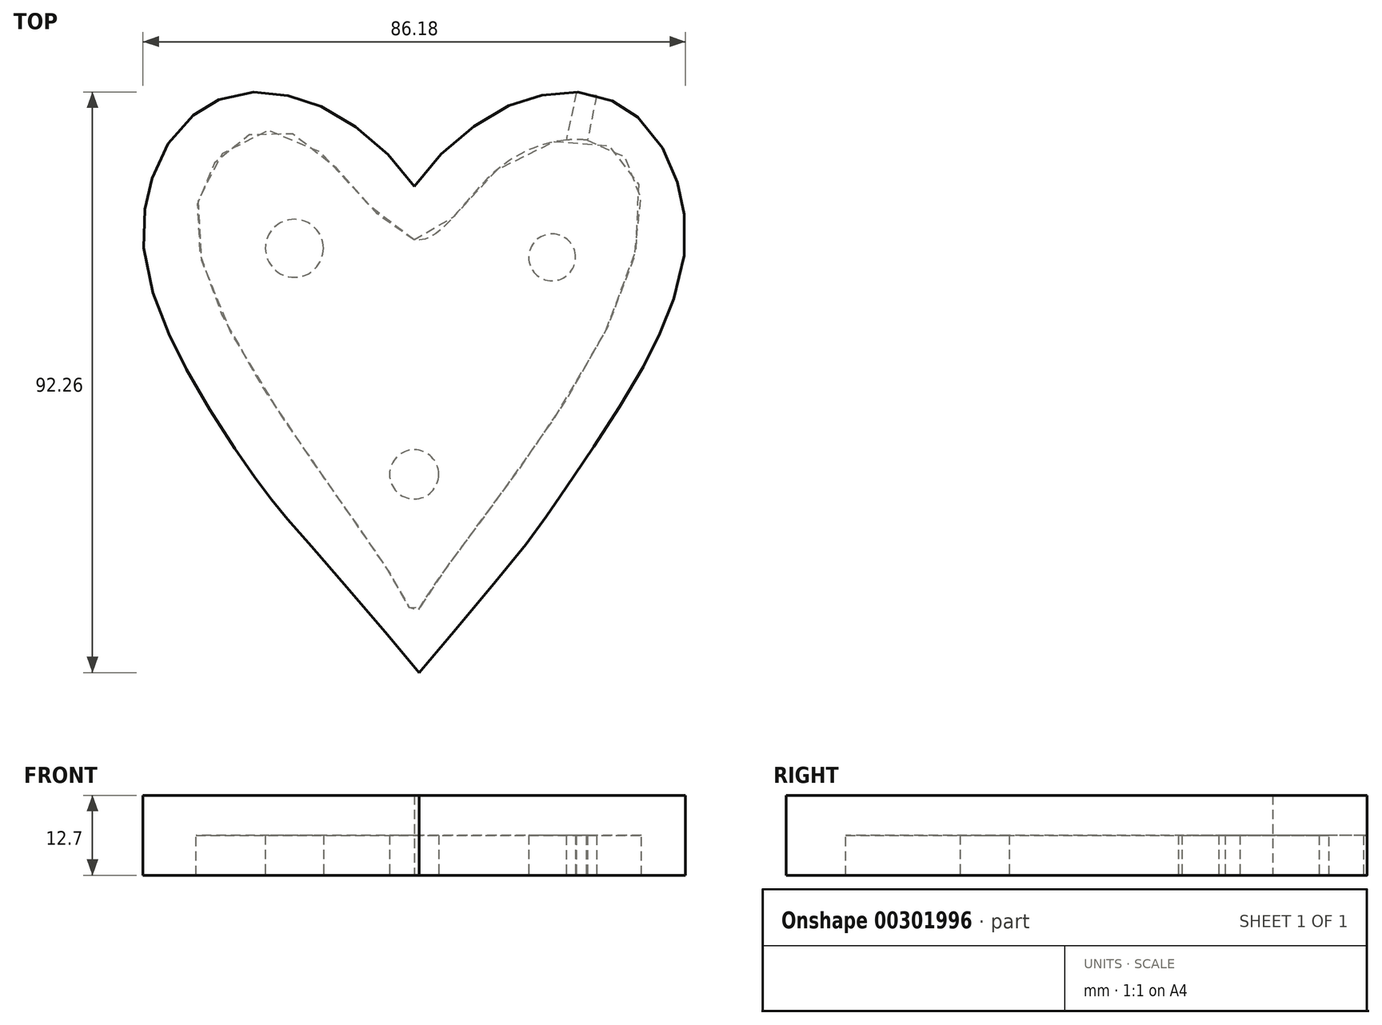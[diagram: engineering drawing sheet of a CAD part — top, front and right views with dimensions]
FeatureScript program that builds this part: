
annotation { "Feature Type Name" : "Feature", "Feature Type Description" : "" }
export const myFeature = defineFeature(function(context is Context, id is Id, definition is map)
    precondition{}
    {
        {
            var Q0;
            Q0=qCreatedBy(makeId("Top.planeOp"),FACE);
            var sketch = newSketch(context, id + "F0", { "sketchPlane" : qUnion([Q0])});
            skFitSpline(sketch, "E0.0", {"points": [v(0.86, 28.46) * mm, v(-0.35, 30.42) * mm, v(-2.59, 33.28) * mm, v(-6.12, 36.72) * mm, v(-8.95, 39.04) * mm, v(-11.94, 41.05) * mm, v(-15.1, 42.7) * mm, v(-17.9, 43.73) * mm, v(-20.24, 44.3) * mm, v(-22.65, 44.72) * mm, v(-25.75, 44.85) * mm, v(-28.85, 44.38) * mm, v(-31.25, 43.54) * mm, v(-33, 42.67) * mm, v(-34.64, 41.54) * mm, v(-36.67, 39.72) * mm, v(-38.89, 36.96) * mm, v(-40.63, 33.71) * mm, v(-41.7, 30.93) * mm, v(-42.31, 28.78) * mm, v(-42.74, 26.58) * mm, v(-43.05, 23.62) * mm, v(-42.96, 19.88) * mm, v(-42.17, 15.33) * mm, v(-40.76, 10.68) * mm, v(-39.13, 6.72) * mm, v(-37.58, 3.5) * mm, v(-35.9, 0.23) * mm, v(-33.58, -3.85) * mm, v(-30.66, -8.55) * mm, v(-28.28, -12.14) * mm, v(-26.49, -14.72) * mm, v(-25.23, -16.49) * mm, v(-24.07, -18.07) * mm, v(-23.06, -19.42) * mm, v(-22.13, -20.6) * mm, v(-21.23, -21.72) * mm, v(-20.28, -22.84) * mm, v(-18.89, -24.45) * mm, v(-16.73, -26.9) * mm, v(-12.94, -31.24) * mm, v(-7.44, -37.65) * mm, v(-2.27, -43.76) * mm, v(0.77, -47.39) * mm]});
            skFitSpline(sketch, "E0.1", {"points": [v(-0.86, 28.46) * mm, v(0.35, 30.42) * mm, v(2.58, 33.28) * mm, v(6.1, 36.7) * mm, v(8.92, 39.02) * mm, v(11.9, 41.03) * mm, v(15.05, 42.68) * mm, v(17.84, 43.71) * mm, v(20.17, 44.3) * mm, v(22.57, 44.7) * mm, v(25.66, 44.86) * mm, v(28.76, 44.4) * mm, v(31.16, 43.58) * mm, v(32.9, 42.73) * mm, v(34.54, 41.61) * mm, v(36.57, 39.82) * mm, v(38.8, 37.08) * mm, v(40.55, 33.86) * mm, v(41.63, 31.1) * mm, v(42.26, 28.95) * mm, v(42.72, 26.76) * mm, v(43.05, 23.8) * mm, v(43, 20.08) * mm, v(42.26, 15.53) * mm, v(41.1, 11.68) * mm, v(39.9, 8.54) * mm, v(38.87, 6.16) * mm, v(37.7, 3.75) * mm, v(36, 0.5) * mm, v(33.64, -3.56) * mm, v(30.68, -8.24) * mm, v(28.3, -11.84) * mm, v(26.52, -14.44) * mm, v(25.3, -16.23) * mm, v(24.4, -17.56) * mm, v(23.74, -18.52) * mm, v(23.14, -19.4) * mm, v(22.47, -20.42) * mm, v(21.7, -21.56) * mm, v(20.91, -22.72) * mm, v(19.73, -24.38) * mm, v(17.83, -26.89) * mm, v(14.31, -31.26) * mm, v(8.99, -37.68) * mm, v(3.84, -43.77) * mm, v(0.77, -47.39) * mm]});
            skPoint(sketch, "E1.0.internal.orphan", {"position": v(0, 27.92) * mm});
            skPoint(sketch, "E1.end.orphan", {"position": v(0, -46.73) * mm});
            skPoint(sketch, "E2.0.internal.orphan", {"position": v(0, 21.62) * mm});
            skPoint(sketch, "E2.5.internal.orphan", {"position": v(0, -38.16) * mm});
            skPoint(sketch, "E2.6.internal.orphan", {"position": v(27.53, 0) * mm});
            skSolve(sketch);
        }
        {
            var Q0;
            Q0=makeQuery(id+"F0.imprint","IMPRINT",FACE,{"disambiguationData":[TD([[makeQuery(id+"F0.imprint","IMPRINT",EDGE,{"derivedFrom":sQuery(id+"F0.wireOp",EDGE,"E0.0")}),1.0]])]});
            var sketch = newSketch(context, id + "F1", { "sketchPlane" : qUnion([Q0])});
            skFitSpline(sketch, "E3", {"points": [v(0, 21.34) * mm, v(-18.96, 38.06) * mm, v(-32.58, 32.3) * mm, v(-30.2, 8.7) * mm, v(-2.67, -33.57) * mm, v(0, -37.92) * mm, v(2.95, -33.85) * mm, v(31.32, 8.7) * mm, v(33, 34.97) * mm, v(14.33, 33.42) * mm, v(0, 21.34) * mm]});
            skCircle(sketch, "E4", {"center": v(21.91, 18.58) * mm, "radius": 3.72 * mm});
            skCircle(sketch, "E5", {"center": v(0, -15.9) * mm, "radius": 3.9 * mm});
            skCircle(sketch, "E6", {"center": v(-19.03, 20.03) * mm, "radius": 4.6 * mm});
            skSolve(sketch);
        }
        {
            var Q0;
            Q0 = qSketchRegion(id + "F0", true);
            extrude(context, id + "F2", {"entities" : qUnion([Q0]), "depth" : 12.7 * mm});
        }
        {
            var Q0;
            Q0 = qSketchRegion(id + "F1", true);
            extrude(context, id + "F3", {"entities" : qUnion([Q0]), "operationType" : NewBodyOperationType.REMOVE, "depth" : 6.35 * mm});
        }
        {
            var Q0;
            Q0=makeQuery(id+"F0.imprint","IMPRINT",FACE,{"disambiguationData":[TD([[makeQuery(id+"F0.imprint","IMPRINT",EDGE,{"derivedFrom":sQuery(id+"F0.wireOp",EDGE,"E0.0")}),1.0]])]});
            var sketch = newSketch(context, id + "F4", { "sketchPlane" : qUnion([Q0])});
            skLineSegment(sketch, "E7", {"start": v(28.96, 44.27) * mm, "end": v(27.53, 37.22) * mm});
            skLineSegment(sketch, "E8", {"start": v(25.75, 44.74) * mm, "end": v(24.13, 37.2) * mm});
            skLineSegment(sketch, "E9", {"start": v(27.53, 37.22) * mm, "end": v(24.13, 37.2) * mm});
            skLineSegment(sketch, "E10", {"start": v(28.96, 44.27) * mm, "end": v(25.75, 44.74) * mm});
            skSolve(sketch);
        }
        {
            var Q0;
            Q0 = qSketchRegion(id + "F4", true);
            extrude(context, id + "F5", {"entities" : qUnion([Q0]), "operationType" : NewBodyOperationType.REMOVE, "depth" : 6.3 * mm});
        }
    });
